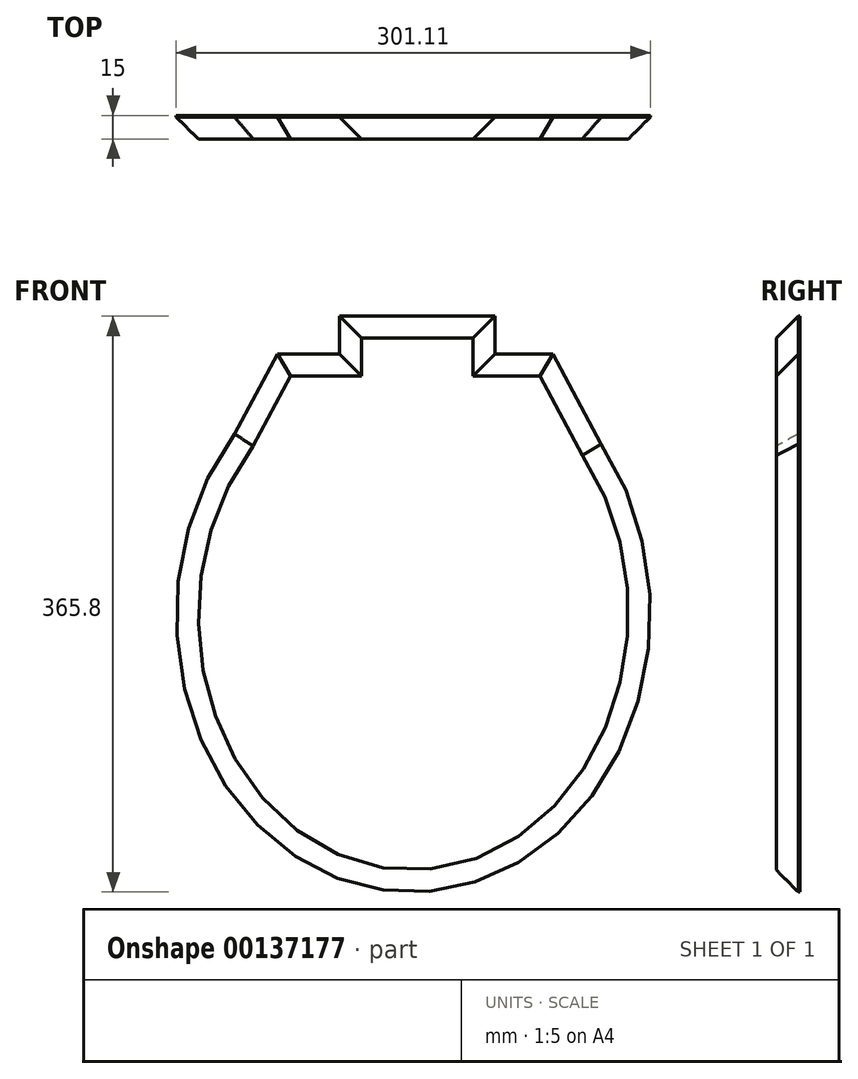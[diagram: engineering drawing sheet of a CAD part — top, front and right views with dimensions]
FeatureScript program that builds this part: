
annotation { "Feature Type Name" : "Feature", "Feature Type Description" : "" }
export const myFeature = defineFeature(function(context is Context, id is Id, definition is map)
    precondition{}
    {
        {
            var Q0;
            Q0=qCreatedBy(makeId("Front.planeOp"),FACE);
            var sketch = newSketch(context, id + "F0", { "sketchPlane" : qUnion([Q0])});
            skPoint(sketch, "E0.centerSnap0", {"position": v(-59.02, 183.96) * mm});
            skEllipticalArc(sketch, "E1", {});
            skLineSegment(sketch, "E2.bottom", {"start": v(-109.74, 197.51) * mm, "end": v(-10.88, 197.51) * mm});
            skLineSegment(sketch, "E2.left", {"start": v(-109.74, 197.51) * mm, "end": v(-109.74, 173.61) * mm});
            skLineSegment(sketch, "E2.right", {"start": v(-10.88, 197.51) * mm, "end": v(-10.88, 173.61) * mm});
            skLineSegment(sketch, "E3.bottom", {"start": v(26.04, 173.61) * mm, "end": v(-10.88, 173.61) * mm});
            skLineSegment(sketch, "E4", {"start": v(-149.03, 173.61) * mm, "end": v(-176.29, 122.62) * mm});
            skLineSegment(sketch, "E5", {"start": v(26.04, 173.61) * mm, "end": v(56.58, 116.19) * mm});
            skLineSegment(sketch, "E6.trimOffspring", {"start": v(-109.74, 173.61) * mm, "end": v(-149.03, 173.61) * mm});
            const initialGuessF0  = {"E1": [-0.06273499131202698, 0.007850917056202888, 0.02106683056053192, 0.9997780696985377, 0.1761490754718741, 0.15053849867944874, 0.8791357047266345, 5.392876675103471]};
            skSetInitialGuess(sketch, initialGuessF0);
            skSolve(sketch);
        }
        {
            var Q0;
            Q0=makeQuery(id+"F0.imprint","IMPRINT",FACE,{"disambiguationData":[TD([[makeQuery(id+"F0.imprint","IMPRINT",EDGE,{"derivedFrom":sQuery(id+"F0.wireOp",EDGE,"E1")}),1.0]])]});
            extrude(context, id + "F1", {"entities" : qUnion([Q0]), "depth" : 15 * mm});
        }
        {
            var Q0;
            Q0=makeQuery(id+"F1.opExtrude","CAP_EDGE",EDGE,{"disambiguationData":[OSD([sQuery(id+"F0.wireOp",EDGE,"E1")])],"isStart":false});
            var Q1;
            Q1=makeQuery(id+"F1.opExtrude","CAP_EDGE",EDGE,{"disambiguationData":[OSD([sQuery(id+"F0.wireOp",EDGE,"E5")])],"isStart":false});
            var Q2;
            Q2=makeQuery(id+"F1.opExtrude","CAP_EDGE",EDGE,{"disambiguationData":[OSD([sQuery(id+"F0.wireOp",EDGE,"E3.bottom")])],"isStart":false});
            var Q3;
            Q3=makeQuery(id+"F1.opExtrude","CAP_EDGE",EDGE,{"disambiguationData":[OSD([sQuery(id+"F0.wireOp",EDGE,"E2.right")])],"isStart":false});
            var Q4;
            Q4=makeQuery(id+"F1.opExtrude","CAP_EDGE",EDGE,{"disambiguationData":[OSD([sQuery(id+"F0.wireOp",EDGE,"E2.bottom")])],"isStart":false});
            var Q5;
            Q5=makeQuery(id+"F1.opExtrude","CAP_EDGE",EDGE,{"disambiguationData":[OSD([sQuery(id+"F0.wireOp",EDGE,"E2.left")])],"isStart":false});
            var Q6;
            Q6=makeQuery(id+"F1.opExtrude","CAP_EDGE",EDGE,{"disambiguationData":[OSD([sQuery(id+"F0.wireOp",EDGE,"E6.trimOffspring")])],"isStart":false});
            var Q7;
            Q7=makeQuery(id+"F1.opExtrude","CAP_EDGE",EDGE,{"disambiguationData":[OSD([sQuery(id+"F0.wireOp",EDGE,"E4")])],"isStart":false});
            chamfer(context, id + "F2", {"entities" : qUnion([Q0, Q1, Q2, Q3, Q4, Q5, Q6, Q7]), "width" : 14 * mm, "tangentPropagation" : true});
        }
    });
